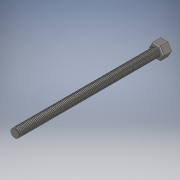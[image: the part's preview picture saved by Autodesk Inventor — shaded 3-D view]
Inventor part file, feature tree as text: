
AUTODESK INVENTOR PART (.ipt)
format: ipt  version: 2019 (Build 230136000, 136)  size: 875,008 bytes
history: native  units: mm
features: sketch x3, extrude x2, helix x1, fillet x1
ambient origin geometry x8: Origin, YZ Plane, XZ Plane, XY Plane, X Axis, Y Axis, Z Axis, Center Point
bodies: Solid1 (feature_tree)
feature tree (7):
  extrude  "Extrusion1"  Depth=118.75mm TaperAngle=0.0deg
  extrude  "Extrusion2"  Depth=7.5mm
  helix  "Coil1"  [1 undecoded]
  fillet  "Fillet1"  Radius=0.5mm
  sketch  "Sketch1"  dims[d0=7.0mm d1=118.75mm d2=0.0mm]
  sketch  "Sketch2"  dims[d3=12.4mm d4=5.369358mm d5=7.5mm d6=0.0mm d7=0.5mm]
  sketch  "Sketch3"  dims[d8=0.5mm d9=10.0mm d10=118.75mm d11=1000.0mm d12=0.0mm d13=90.0deg d14=90.0deg d15=0.0mm d16=0.0mm d17=0.8mm]
note: 1 required parameter value undecoded (feature->parameter linkage not recoverable at this tier; creation-order binding heuristic only, values carry confidence <= 0.55)
